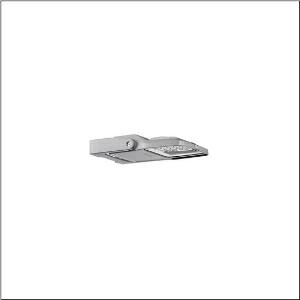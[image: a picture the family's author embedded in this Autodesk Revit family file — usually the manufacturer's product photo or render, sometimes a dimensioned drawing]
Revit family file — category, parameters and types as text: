
# Revit family: floodlight_fl_21_iq_micro___pl52_5xa7762a4d2a_e4f8
name_source: partatom
category: Lighting Fixtures
units: mm (PartAtom-declared; Revit-internal decimal feet)

## family parameters
Cut with Voids When Loaded = No
Host = Face
Light Source = No
Part Type = Normal
Room Calculation Point = No
Round Connector Dimension = Use Diameter
Shared = No

## types (1)
- --- (1 x LED, 3010 lm, 23.1 W, 4000K)
    Apparent Load = 23 VA
    CIE Flux Codes = 26 60 98 100 100
    Color Rendering = 70
    Color Temperature = 4000K
    Default Elevation = 1800 mm
    Description = Floodlight FL 21 iQ micro, floodlight, primary light control with lens, of PMMA, primary optical cover: protective disc, of toughened safety glass, transparent, light distribution: PL52, light emission: direct distribution, installation type: surface-mounted, LED, High Power LED, rated luminous flux: 3.010lm, luminous efficacy: 130lm/W, light colour: 740, colour temperature: 4000K, control: Auto-Match, Temp-Guard, Night-Set, Smart-Wire, Desk-Remote (wireless, voltage-free reading and setting of iQ features in the workshop via application-optimized NFC function/RFID function), optimised constant luminous flux control (CLO 2.0), Street-Remote, with terminal, 6-pole, mains connection: 220..240V, AC, 50/60Hz, start of lifetime: 23W, end of service life: 24W, reduction: 11W, luminaire housing, of diecast aluminium, powder-coated, Siteco® metallic grey (DB 702S), corrosivity category C5 mid according to DIN EN ISO 12944, sealing non-destructively replaceable, design bracket, of diecast aluminium, powder-coated, Siteco® metallic grey (DB 702S), protection rating (complete): IP66, insulation class (complete): insulation class II (safety insulation), certification: CE, ENEC, VDE, protection symbol: D, impact resistance: IK07, permissible operating ambient temperature: -40..+40°C, permissible operating ambient temperature for outdoor applications: -40..+50°C, standard: DIN EN 12944, LABS conformity tested according to VDMA 24364:2018-05, packaging unit: 1 piece

Light Distribution: PL52
    Height = 65 mm
    Lamp = 1 x LED
    Lamp Light Flux = 3010 lm
    Lamp Power = 23.1 W
    Lamp count = 1
    Length = 312 mm
    Luminous efficacy = 130 lm/W
    Manufacturer = Siteco
    ModVariant = No
    Model = 5XA7762A4D2A
    Mounting Place = Wall
    Mounting Type = Surface mounted
    Number of Poles = 1
    OnlyDefault = Yes
    Power Factor = 1
    Product Name = Floodlight FL 21 iQ micro | PL52
    Product group = floodlight | wall mounted
    ProductGroupID = 2001
    Protection Class = Protection class II
    Protection Degree = IP 66
    RLX_Detail_Level = 1
    RLX_Emergency_Light_Flux = 0 lm
    RLX_Emergency_Type = 0
    RLX_Emergency_Type_DB = No
    RlxData = <blob elided: 97497 chars, md5=5ac78cee>
    Socket = socket
    Standby Power = 0 W
    System Light Flux = 3010 lm
    System Power = 23 W
    Type Comments = factory setting: luminous flux: 100 % | dim-lin: 254 | 455 mA
    Type Image = l_1006878.jpg
    URL = http://relux.com
    VarID = @adj_128959
    Voltage = 0 V
    Weight = 0.00 kg
    Width = 230 mm

## geometry (parser evidence)
native form markers: Blend x4, Sweep x11
no freeform markers — native parametric forms only
